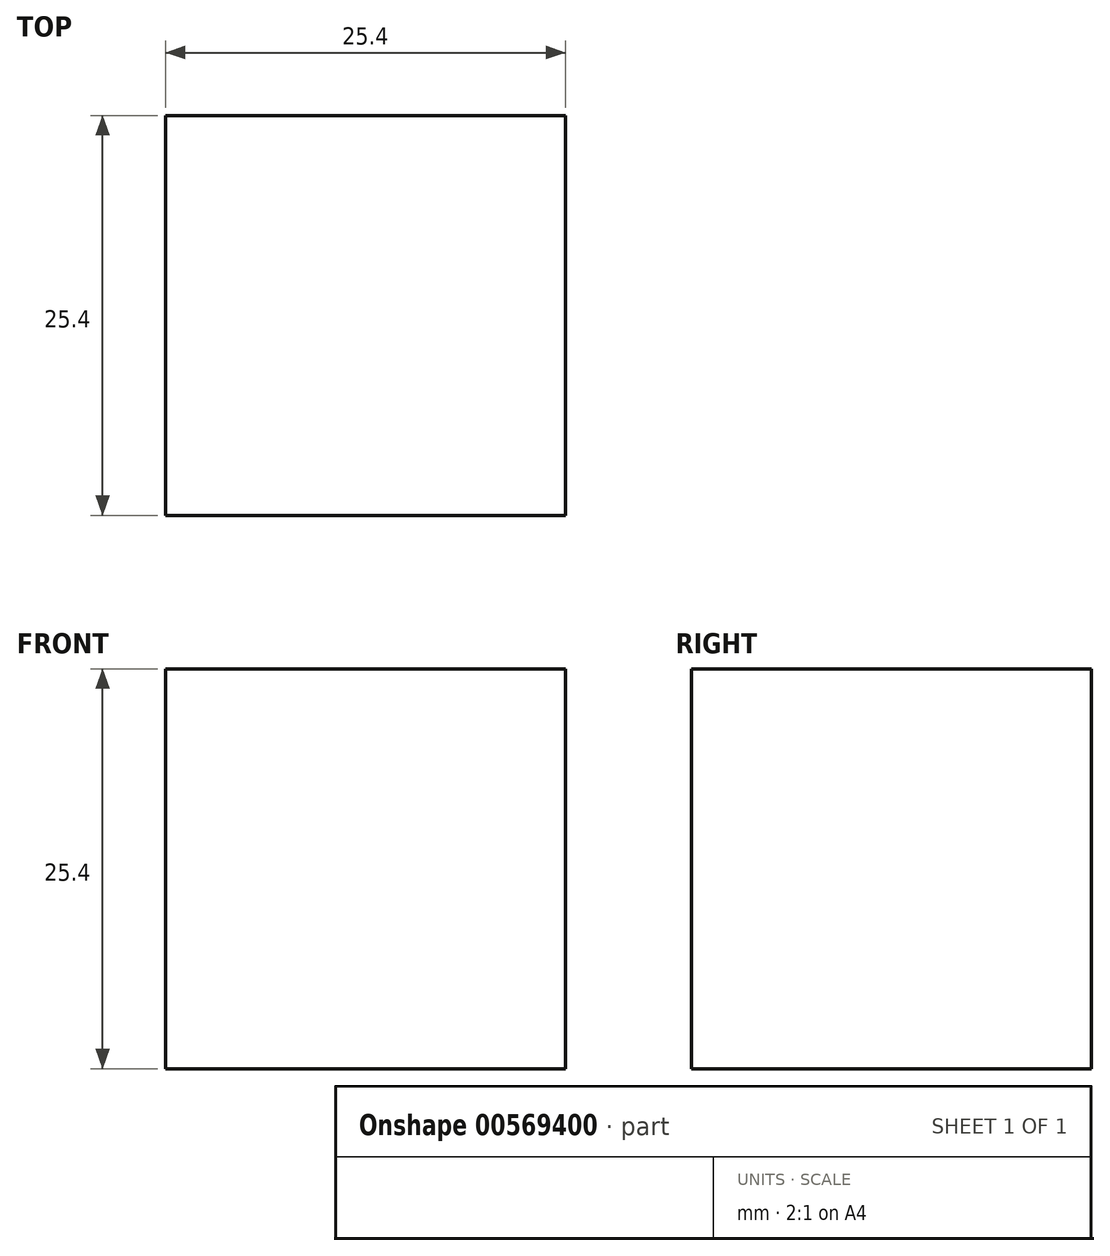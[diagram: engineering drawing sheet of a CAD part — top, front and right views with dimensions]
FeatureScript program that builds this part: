
annotation { "Feature Type Name" : "Feature", "Feature Type Description" : "" }
export const myFeature = defineFeature(function(context is Context, id is Id, definition is map)
    precondition{}
    {
        {
            var Q0;
            Q0=qCreatedBy(makeId("Front.planeOp"),FACE);
            var sketch = newSketch(context, id + "F0", { "sketchPlane" : qUnion([Q0])});
            skLineSegment(sketch, "E0", {"start": v(-12.7, -12.7) * mm, "end": v(0, -12.7) * mm});
            skLineSegment(sketch, "E1", {"start": v(0, -12.7) * mm, "end": v(12.7, -12.7) * mm});
            skLineSegment(sketch, "E2", {"start": v(-12.7, -12.7) * mm, "end": v(-12.7, 12.7) * mm});
            skLineSegment(sketch, "E3", {"start": v(-12.7, 12.7) * mm, "end": v(12.7, 12.7) * mm});
            skLineSegment(sketch, "E4", {"start": v(12.7, 12.7) * mm, "end": v(12.7, -12.7) * mm});
            skLineSegment(sketch, "E5", {"start": v(-12.7, 12.7) * mm, "end": v(0, 0) * mm, "construction": true});
            skLineSegment(sketch, "E6", {"start": v(0, 0) * mm, "end": v(-12.7, -12.7) * mm, "construction": true});
            skLineSegment(sketch, "E7", {"start": v(12.7, 12.7) * mm, "end": v(0, 0) * mm, "construction": true});
            skLineSegment(sketch, "E8", {"start": v(0, 0) * mm, "end": v(0, -12.7) * mm, "construction": true});
            skSolve(sketch);
        }
        {
            var Q0;
            Q0 = qSketchRegion(id + "F0", true);
            extrude(context, id + "F1", {"entities" : qUnion([Q0]), "depth" : 25.4 * mm, "offsetDistance" : 25.4 * mm});
        }
    });
